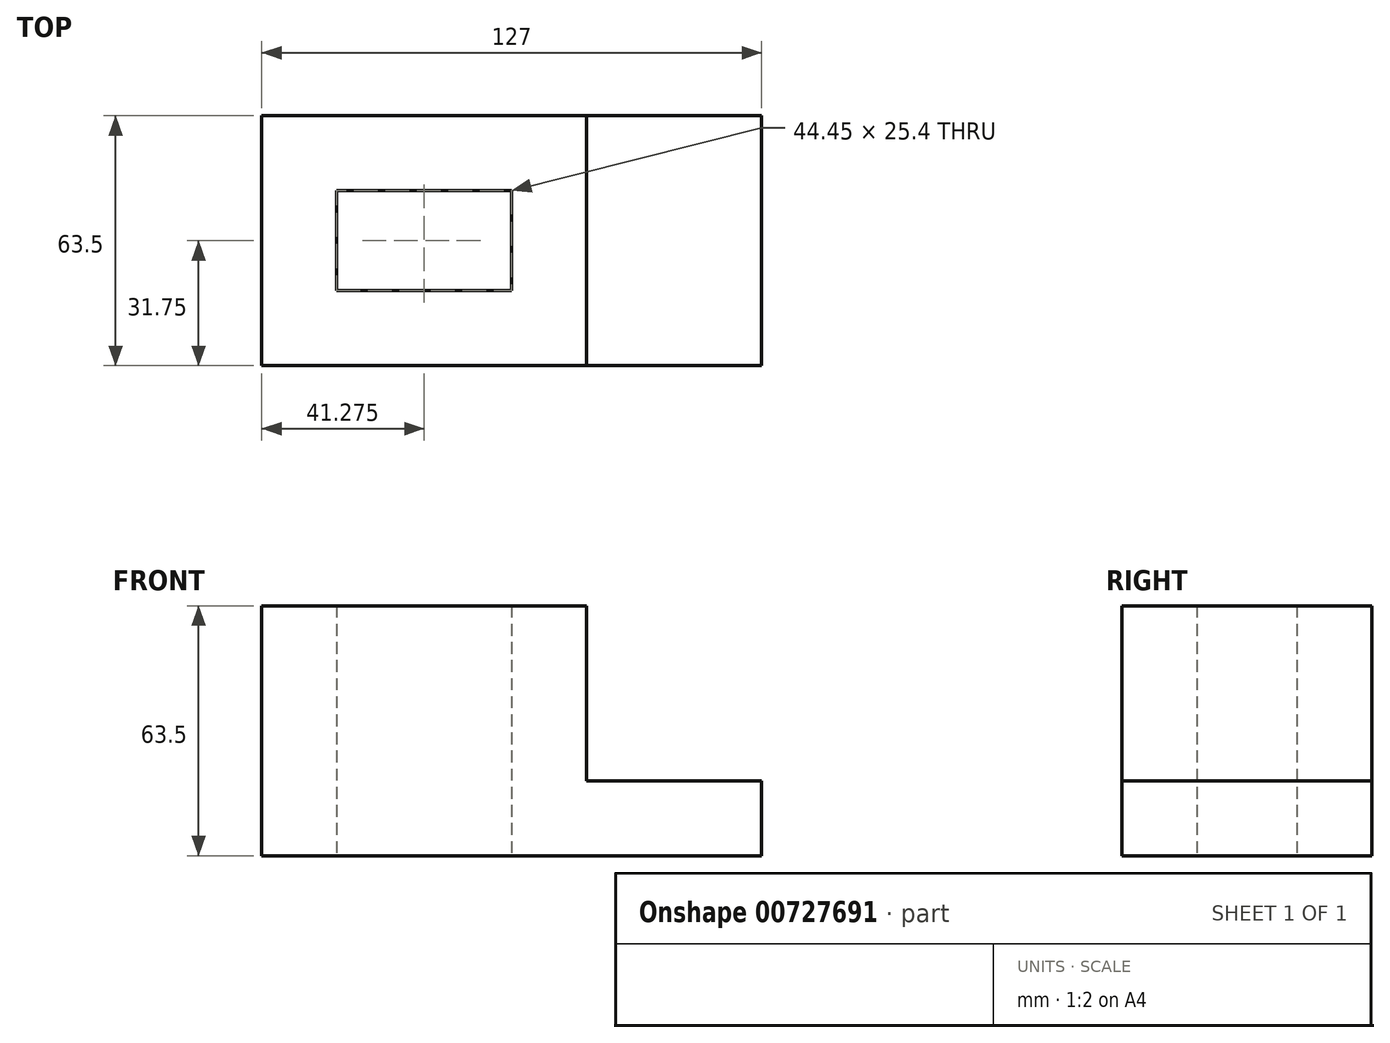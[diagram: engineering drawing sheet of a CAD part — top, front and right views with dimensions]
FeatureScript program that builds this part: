
annotation { "Feature Type Name" : "Feature", "Feature Type Description" : "" }
export const myFeature = defineFeature(function(context is Context, id is Id, definition is map)
    precondition{}
    {
        {
            var Q0;
            Q0=qCreatedBy(makeId("Top.planeOp"),FACE);
            var sketch = newSketch(context, id + "F0", { "sketchPlane" : qUnion([Q0])});
            skLineSegment(sketch, "E0", {"start": v(0, 0) * mm, "end": v(-82.55, 0) * mm});
            skLineSegment(sketch, "E1", {"start": v(-82.55, 0) * mm, "end": v(-82.55, 63.5) * mm});
            skLineSegment(sketch, "E2", {"start": v(-82.55, 63.5) * mm, "end": v(0, 63.5) * mm});
            skLineSegment(sketch, "E3", {"start": v(0, 63.5) * mm, "end": v(0, 0) * mm});
            skLineSegment(sketch, "E4.bottom", {"start": v(-63.5, 44.45) * mm, "end": v(-19.05, 44.45) * mm});
            skLineSegment(sketch, "E4.top", {"start": v(-63.5, 19.05) * mm, "end": v(-19.05, 19.05) * mm});
            skLineSegment(sketch, "E4.left", {"start": v(-63.5, 44.45) * mm, "end": v(-63.5, 19.05) * mm});
            skLineSegment(sketch, "E4.right", {"start": v(-19.05, 44.45) * mm, "end": v(-19.05, 19.05) * mm});
            skPoint(sketch, "E4.middle", {"position": v(-41.27, 31.75) * mm});
            skSolve(sketch);
        }
        {
            var Q0;
            Q0 = qSketchRegion(id + "F0", true);
            extrude(context, id + "F1", {"entities" : qUnion([Q0]), "depth" : 63.5 * mm, "offsetDistance" : 25.4 * mm});
        }
        {
            var Q0;
            Q0=qCreatedBy(makeId("Top.planeOp"),FACE);
            var sketch = newSketch(context, id + "F2", { "sketchPlane" : qUnion([Q0])});
            skLineSegment(sketch, "E5", {"start": v(0, 63.5) * mm, "end": v(44.45, 63.5) * mm});
            skLineSegment(sketch, "E6", {"start": v(44.45, 63.5) * mm, "end": v(44.45, 0) * mm});
            skLineSegment(sketch, "E7", {"start": v(44.45, 0) * mm, "end": v(0, 0) * mm});
            skLineSegment(sketch, "E8", {"start": v(0, 0) * mm, "end": v(0, 63.5) * mm});
            skSolve(sketch);
        }
        {
            var Q0;
            Q0 = qSketchRegion(id + "F2", true);
            extrude(context, id + "F3", {"entities" : qUnion([Q0]), "operationType" : NewBodyOperationType.ADD, "depth" : 19.05 * mm, "offsetDistance" : 25.4 * mm});
        }
    });
